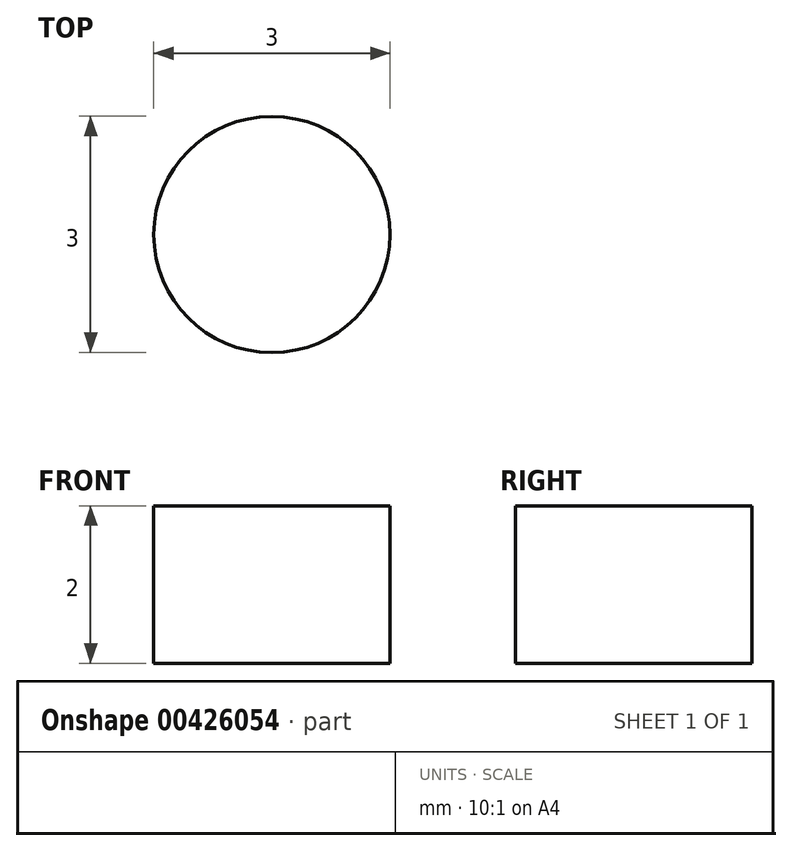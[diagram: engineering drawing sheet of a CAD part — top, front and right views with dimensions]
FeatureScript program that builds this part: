
annotation { "Feature Type Name" : "Feature", "Feature Type Description" : "" }
export const myFeature = defineFeature(function(context is Context, id is Id, definition is map)
    precondition{}
    {
        {
            var Q0;
            Q0=qCreatedBy(makeId("Top.planeOp"),FACE);
            var sketch = newSketch(context, id + "F0", { "sketchPlane" : qUnion([Q0])});
            skCircle(sketch, "E0.MirrorC", {"center": v(-22.01, 38.49) * mm, "radius": 1.5 * mm});
            skCircle(sketch, "E1.MirrorC", {"center": v(27.49, 38.49) * mm, "radius": 1.5 * mm});
            skCircle(sketch, "E2.MirrorC", {"center": v(22.74, -5.12) * mm, "radius": 1.5 * mm});
            skCircle(sketch, "E3.MirrorC", {"center": v(-17.26, -5.12) * mm, "radius": 1.5 * mm});
            skLineSegment(sketch, "E4.bottom", {"start": v(-38.37, 51.3) * mm, "end": v(46.03, 51.3) * mm});
            skLineSegment(sketch, "E4.top", {"start": v(-38.37, -68.99) * mm, "end": v(46.03, -68.99) * mm});
            skLineSegment(sketch, "E4.left", {"start": v(-38.37, 51.3) * mm, "end": v(-38.37, -68.99) * mm});
            skLineSegment(sketch, "E4.right", {"start": v(46.03, 51.3) * mm, "end": v(46.03, -68.99) * mm});
            skSolve(sketch);
        }
        {
            var Q0;
            Q0=makeQuery(id+"F0.imprint","IMPRINT",FACE,{"disambiguationData":[TD([[makeQuery(id+"F0.imprint","IMPRINT",EDGE,{"derivedFrom":sQuery(id+"F0.wireOp",EDGE,"E0.MirrorC")}),1.0]])]});
            extrude(context, id + "F1", {"entities" : qUnion([Q0]), "depth" : 2 * mm});
        }
    });
